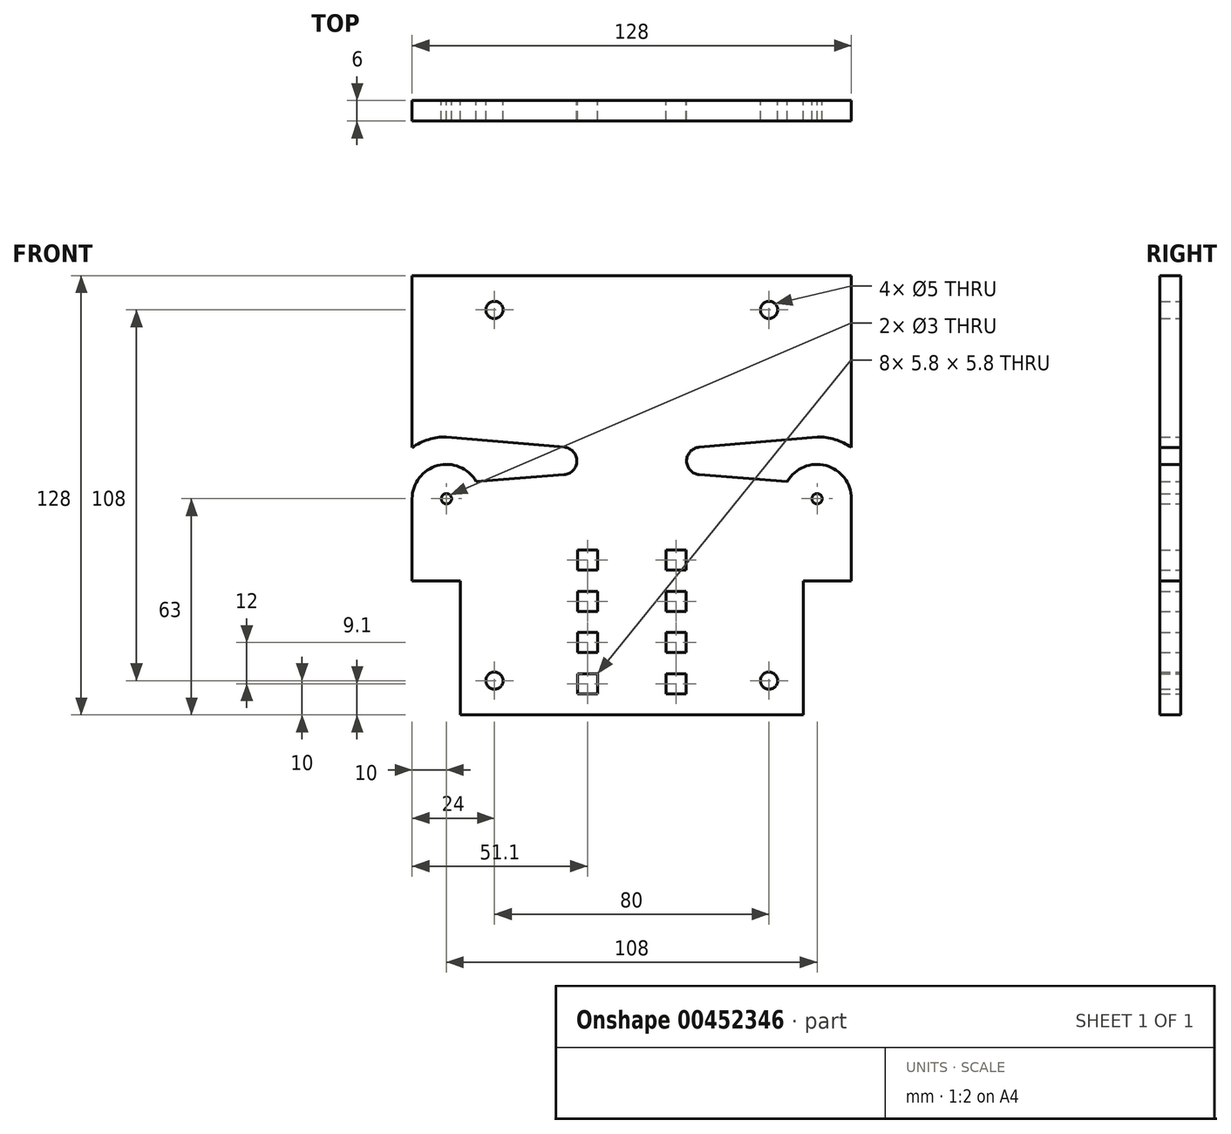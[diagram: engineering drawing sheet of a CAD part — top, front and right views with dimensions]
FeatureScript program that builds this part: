
annotation { "Feature Type Name" : "Feature", "Feature Type Description" : "" }
export const myFeature = defineFeature(function(context is Context, id is Id, definition is map)
    precondition{}
    {
        {
            var Q0;
            Q0=qCreatedBy(makeId("Front.planeOp"),FACE);
            var sketch = newSketch(context, id + "F0", { "sketchPlane" : qUnion([Q0])});
            skLineSegment(sketch, "E0.top", {"start": v(-50, -39) * mm, "end": v(50, -39) * mm});
            skCircle(sketch, "E1", {"center": v(-40, 79) * mm, "radius": 2.5 * mm});
            skCircle(sketch, "E2", {"center": v(-40, -29) * mm, "radius": 2.5 * mm});
            skCircle(sketch, "E3", {"center": v(40, -29) * mm, "radius": 2.5 * mm});
            skCircle(sketch, "E4", {"center": v(40, 79) * mm, "radius": 2.5 * mm});
            skLineSegment(sketch, "E5", {"start": v(64, 0) * mm, "end": v(50, 0) * mm});
            skLineSegment(sketch, "E6", {"start": v(50, 0) * mm, "end": v(50, -39) * mm});
            skLineSegment(sketch, "E7", {"start": v(-50, -39) * mm, "end": v(-50, 0) * mm});
            skLineSegment(sketch, "E8", {"start": v(-50, 0) * mm, "end": v(-64, 0) * mm});
            skCircle(sketch, "E9", {"center": v(-54, 24) * mm, "radius": 1.5 * mm});
            skLineSegment(sketch, "E10", {"start": v(-64, 89) * mm, "end": v(-64, 38.97) * mm});
            skLineSegment(sketch, "E11", {"start": v(-64, 24) * mm, "end": v(-64, 0) * mm});
            skLineSegment(sketch, "E12.bottom", {"start": v(-15.8, -20.8) * mm, "end": v(-10, -20.8) * mm});
            skLineSegment(sketch, "E12.top", {"start": v(-15.8, -15) * mm, "end": v(-10, -15) * mm});
            skLineSegment(sketch, "E12.left", {"start": v(-15.8, -20.8) * mm, "end": v(-15.8, -15) * mm});
            skLineSegment(sketch, "E12.right", {"start": v(-10, -20.8) * mm, "end": v(-10, -15) * mm});
            skLineSegment(sketch, "E13.bottom", {"start": v(-15.8, -8.8) * mm, "end": v(-10, -8.8) * mm});
            skLineSegment(sketch, "E13.top", {"start": v(-15.8, -3) * mm, "end": v(-10, -3) * mm});
            skLineSegment(sketch, "E13.left", {"start": v(-15.8, -8.8) * mm, "end": v(-15.8, -3) * mm});
            skLineSegment(sketch, "E13.right", {"start": v(-10, -8.8) * mm, "end": v(-10, -3) * mm});
            skLineSegment(sketch, "E14.bottom", {"start": v(-15.8, 3.2) * mm, "end": v(-10, 3.2) * mm});
            skLineSegment(sketch, "E14.top", {"start": v(-15.8, 9) * mm, "end": v(-10, 9) * mm});
            skLineSegment(sketch, "E14.left", {"start": v(-15.8, 3.2) * mm, "end": v(-15.8, 9) * mm});
            skLineSegment(sketch, "E14.right", {"start": v(-10, 3.2) * mm, "end": v(-10, 9) * mm});
            skLineSegment(sketch, "E15.bottom", {"start": v(10, -20.8) * mm, "end": v(15.8, -20.8) * mm});
            skLineSegment(sketch, "E15.top", {"start": v(10, -15) * mm, "end": v(15.8, -15) * mm});
            skLineSegment(sketch, "E15.left", {"start": v(10, -20.8) * mm, "end": v(10, -15) * mm});
            skLineSegment(sketch, "E15.right", {"start": v(15.8, -20.8) * mm, "end": v(15.8, -15) * mm});
            skLineSegment(sketch, "E16.bottom", {"start": v(10, -8.8) * mm, "end": v(15.8, -8.8) * mm});
            skLineSegment(sketch, "E16.top", {"start": v(10, -3) * mm, "end": v(15.8, -3) * mm});
            skLineSegment(sketch, "E16.left", {"start": v(10, -8.8) * mm, "end": v(10, -3) * mm});
            skLineSegment(sketch, "E16.right", {"start": v(15.8, -8.8) * mm, "end": v(15.8, -3) * mm});
            skLineSegment(sketch, "E17.bottom", {"start": v(10, 3.2) * mm, "end": v(15.8, 3.2) * mm});
            skLineSegment(sketch, "E17.top", {"start": v(10, 9) * mm, "end": v(15.8, 9) * mm});
            skLineSegment(sketch, "E17.left", {"start": v(10, 3.2) * mm, "end": v(10, 9) * mm});
            skLineSegment(sketch, "E17.right", {"start": v(15.8, 3.2) * mm, "end": v(15.8, 9) * mm});
            skLineSegment(sketch, "E18", {"start": v(-64, 89) * mm, "end": v(64, 89) * mm});
            skLineSegment(sketch, "E19.bottom", {"start": v(-15.8, -27) * mm, "end": v(-10, -27) * mm});
            skLineSegment(sketch, "E19.top", {"start": v(-15.8, -32.8) * mm, "end": v(-10, -32.8) * mm});
            skLineSegment(sketch, "E19.left", {"start": v(-15.8, -27) * mm, "end": v(-15.8, -32.8) * mm});
            skLineSegment(sketch, "E19.right", {"start": v(-10, -27) * mm, "end": v(-10, -32.8) * mm});
            skLineSegment(sketch, "E20.bottom", {"start": v(10, -27) * mm, "end": v(15.8, -27) * mm});
            skLineSegment(sketch, "E20.top", {"start": v(10, -32.8) * mm, "end": v(15.8, -32.8) * mm});
            skLineSegment(sketch, "E20.left", {"start": v(10, -27) * mm, "end": v(10, -32.8) * mm});
            skLineSegment(sketch, "E20.right", {"start": v(15.8, -27) * mm, "end": v(15.8, -32.8) * mm});
            skArc(sketch, "E21", {"start": v(-64, 24) * mm, "mid": v(-56.59, 33.66) * mm, "end": v(-45.34, 29) * mm});
            skArc(sketch, "E22", {"start": v(-64, 38.97) * mm, "mid": v(-59.22, 41.22) * mm, "end": v(-54, 42) * mm});
            skLineSegment(sketch, "E23.MirrorCS", {"start": v(64, 89) * mm, "end": v(64, 38.97) * mm});
            skLineSegment(sketch, "E24.MirrorCS", {"start": v(64, 24) * mm, "end": v(64, 0) * mm});
            skLineSegment(sketch, "E25", {"start": v(-54, 42) * mm, "end": v(-19.65, 38.98) * mm});
            skLineSegment(sketch, "E26", {"start": v(-19.69, 31.01) * mm, "end": v(-45.34, 29) * mm});
            skArc(sketch, "E27", {"start": v(-19.65, 38.98) * mm, "mid": v(-16, 34.98) * mm, "end": v(-19.69, 31.01) * mm});
            skLineSegment(sketch, "E28", {"start": v(-54, 24) * mm, "end": v(-64, 24) * mm, "construction": true});
            skLineSegment(sketch, "E29", {"start": v(-45.34, 29) * mm, "end": v(-54, 24) * mm, "construction": true});
            skCircle(sketch, "E30.MirrorC", {"center": v(54, 24) * mm, "radius": 1.5 * mm});
            skArc(sketch, "E31.MirrorCS", {"start": v(64, 38.97) * mm, "mid": v(59.22, 41.22) * mm, "end": v(54, 42) * mm});
            skLineSegment(sketch, "E32.MirrorCS", {"start": v(54, 24) * mm, "end": v(64, 24) * mm, "construction": true});
            skLineSegment(sketch, "E33.MirrorCS", {"start": v(45.34, 29) * mm, "end": v(54, 24) * mm, "construction": true});
            skLineSegment(sketch, "E34.MirrorCS", {"start": v(54, 42) * mm, "end": v(19.65, 38.98) * mm});
            skArc(sketch, "E35.MirrorCS", {"start": v(64, 24) * mm, "mid": v(56.59, 33.66) * mm, "end": v(45.34, 29) * mm});
            skLineSegment(sketch, "E36.MirrorCS", {"start": v(19.69, 31.01) * mm, "end": v(45.34, 29) * mm});
            skArc(sketch, "E37.MirrorCS", {"start": v(19.65, 38.98) * mm, "mid": v(16, 34.98) * mm, "end": v(19.69, 31.01) * mm});
            skSolve(sketch);
        }
        {
            var Q0;
            Q0 = qSketchRegion(id + "F0", true);
            extrude(context, id + "F1", {"entities" : qUnion([Q0]), "depth" : 6 * mm});
        }
    });
